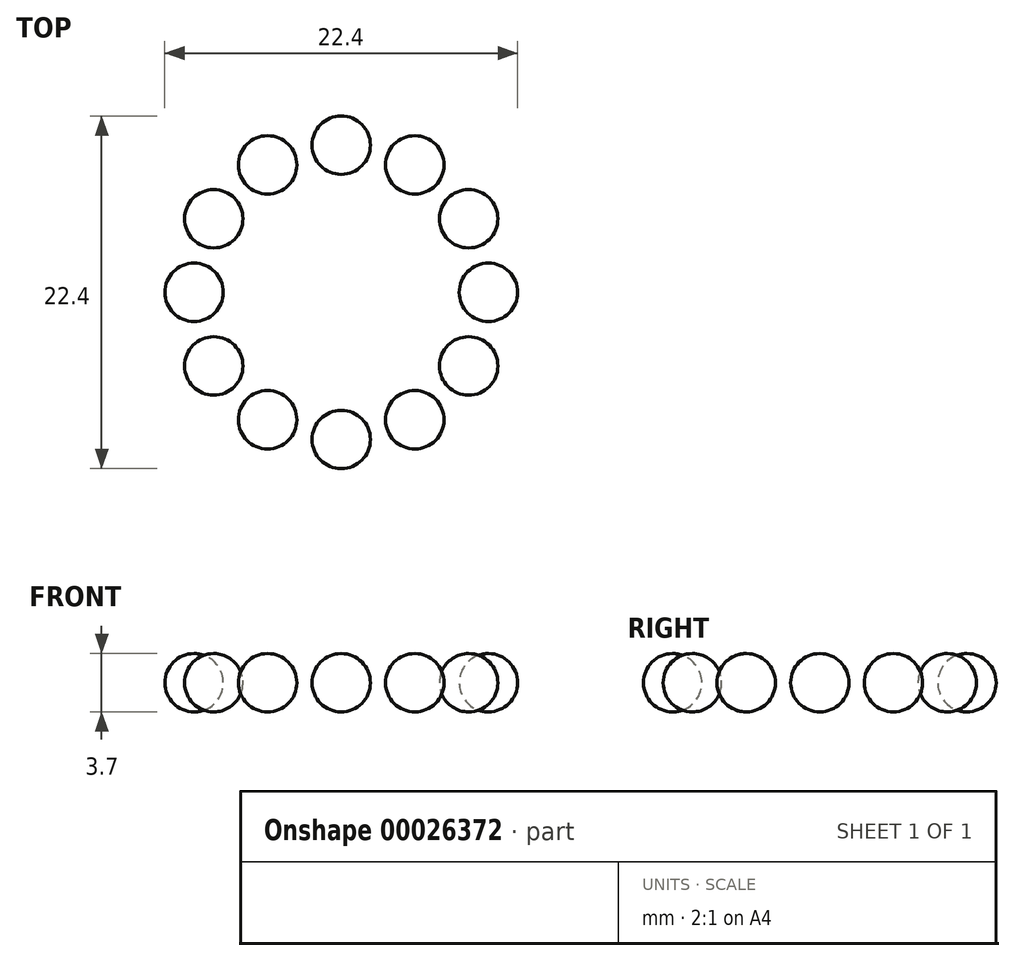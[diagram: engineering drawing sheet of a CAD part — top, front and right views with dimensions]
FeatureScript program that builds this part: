
annotation { "Feature Type Name" : "Feature", "Feature Type Description" : "" }
export const myFeature = defineFeature(function(context is Context, id is Id, definition is map)
    precondition{}
    {
        {
            var Q0;
            Q0=qCreatedBy(makeId("Front.planeOp"),FACE);
            var sketch = newSketch(context, id + "F0", { "sketchPlane" : qUnion([Q0])});
            skArc(sketch, "E0", {"start": v(0, -1.85) * mm, "mid": v(1.85, 0) * mm, "end": v(0, 1.85) * mm});
            skLineSegment(sketch, "E1", {"start": v(0, 5.76) * mm, "end": v(0, -6.25) * mm, "construction": true});
            skLineSegment(sketch, "E2", {"start": v(0, 1.85) * mm, "end": v(0, -1.85) * mm});
            skLineSegment(sketch, "E3", {"start": v(-9.35, 7.1) * mm, "end": v(-9.35, -8.98) * mm});
            skPoint(sketch, "E4", {"position": v(-9.35, 0) * mm});
            skSolve(sketch);
        }
        {
            var Q0;
            Q0=makeQuery(id+"F0.imprint","IMPRINT",FACE,{"disambiguationData":[TD([[makeQuery(id+"F0.imprint","IMPRINT",EDGE,{"derivedFrom":sQuery(id+"F0.wireOp",EDGE,"E0")}),1.0]])]});
            var Q1;
            Q1=sQuery(id+"F0.wireOp",EDGE,"E1");
            revolve(context, id + "F1", {"entities" : qUnion([Q0]), "axis" : qUnion([Q1]), "revolveType" : RevolveType.FULL});
        }
        {
            var Q0;
            Q0=makeQuery(id+"F1.opRevolve","SWEPT_BODY",BODY,{"disambiguationData":[OSD([sQuery(id+"F0.wireOp",EDGE,"E0"),sQuery(id+"F0.wireOp",EDGE,"E2")])]});
            var Q1;
            Q1=sQuery(id+"F0.wireOp",EDGE,"E3");
            circularPattern(context, id + "F2", {"entities" : qUnion([Q0]), "axis" : qUnion([Q1]), "angle" : 360 * degree, "instanceCount" : 12, "equalSpace" : true});
        }
    });
